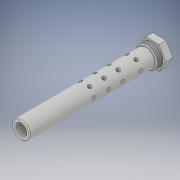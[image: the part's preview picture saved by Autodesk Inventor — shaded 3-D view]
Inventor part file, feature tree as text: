
AUTODESK INVENTOR PART (.ipt)
format: ipt  version: 2019 (Build 230136000, 136)  size: 226,304 bytes
history: native  units: mm
features: sketch x4, other x3, extrude x3, chamfer x2, pattern_circular x2, pattern_linear x1, projected_geometry x1
ambient origin geometry x8: Origin, YZ Plane, XZ Plane, XY Plane, X Axis, Y Axis, Z Axis, Center Point
bodies: Solide1 (feature_tree)
feature tree (16):
  other  "Révolution1"
  other  "Filetage1"
  other  "Filetage2"
  extrude  "Extrusion1"  Depth=12.0mm
  chamfer  "Chanfrein2"  Distance=3.5mm
  extrude  "Extrusion2"  Depth=4.0mm
  extrude  "Extrusion4"  Depth=2.0mm
  chamfer  "Chanfrein3"  Distance=6.0mm
  pattern_circular  "Réseau circulaire2"  [2 undecoded]
  pattern_circular  "Réseau circulaire3"  [2 undecoded]
  pattern_linear  "Réseau rectangulaire2"  Spacing1=4.0mm  [1 undecoded]
  sketch  "Esquisse1"
  sketch  "Esquisse2"
  projected_geometry  "Boucle projetée1"
  sketch  "Esquisse3"
  sketch  "Esquisse5"
note: 5 required parameter values undecoded (feature->parameter linkage not recoverable at this tier; creation-order binding heuristic only, values carry confidence <= 0.55)
